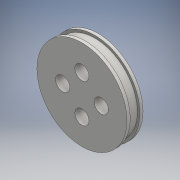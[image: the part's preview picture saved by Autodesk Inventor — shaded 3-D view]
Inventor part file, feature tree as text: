
AUTODESK INVENTOR PART (.ipt)
format: ipt  version: 2016 (Build 200138000, 138)  size: 131,584 bytes
history: native  units: mm
features: sketch x4, extrude x3, hole x1
ambient origin geometry x8: Origin, YZ Plane, XZ Plane, XY Plane, X Axis, Y Axis, Z Axis, Center Point
bodies: Solid1 (feature_tree)
feature tree (8):
  extrude  "Extrusion1"  Depth=1.0mm TaperAngle=0.0deg
  extrude  "Extrusion2"  Depth=3.0mm TaperAngle=0.0deg
  extrude  "Extrusion3"  Depth=1.0mm TaperAngle=0.0deg
  hole  "Hole1"  [1 undecoded]
  sketch  "Sketch1"  dims[d0=28.0mm d1=1.0mm d2=0.0mm]
  sketch  "Sketch2"  dims[d3=26.5mm d4=3.0mm d5=0.0mm]
  sketch  "Sketch3"  dims[d6=28.0mm d7=1.0mm d8=0.0mm]
  sketch  "Sketch4"  dims[d9=4.4mm d10=6.0mm d11=4.4mm d12=12.0mm d13=4.4mm d14=6.0mm d15=4.4mm d16=6.0mm d17=4.4mm d18=6.0mm d19=4.0mm d20=2.0mm d21=90.0deg d22=8.0mm d23=20.594885mm]
note: 1 required parameter value undecoded (feature->parameter linkage not recoverable at this tier; creation-order binding heuristic only, values carry confidence <= 0.55)
